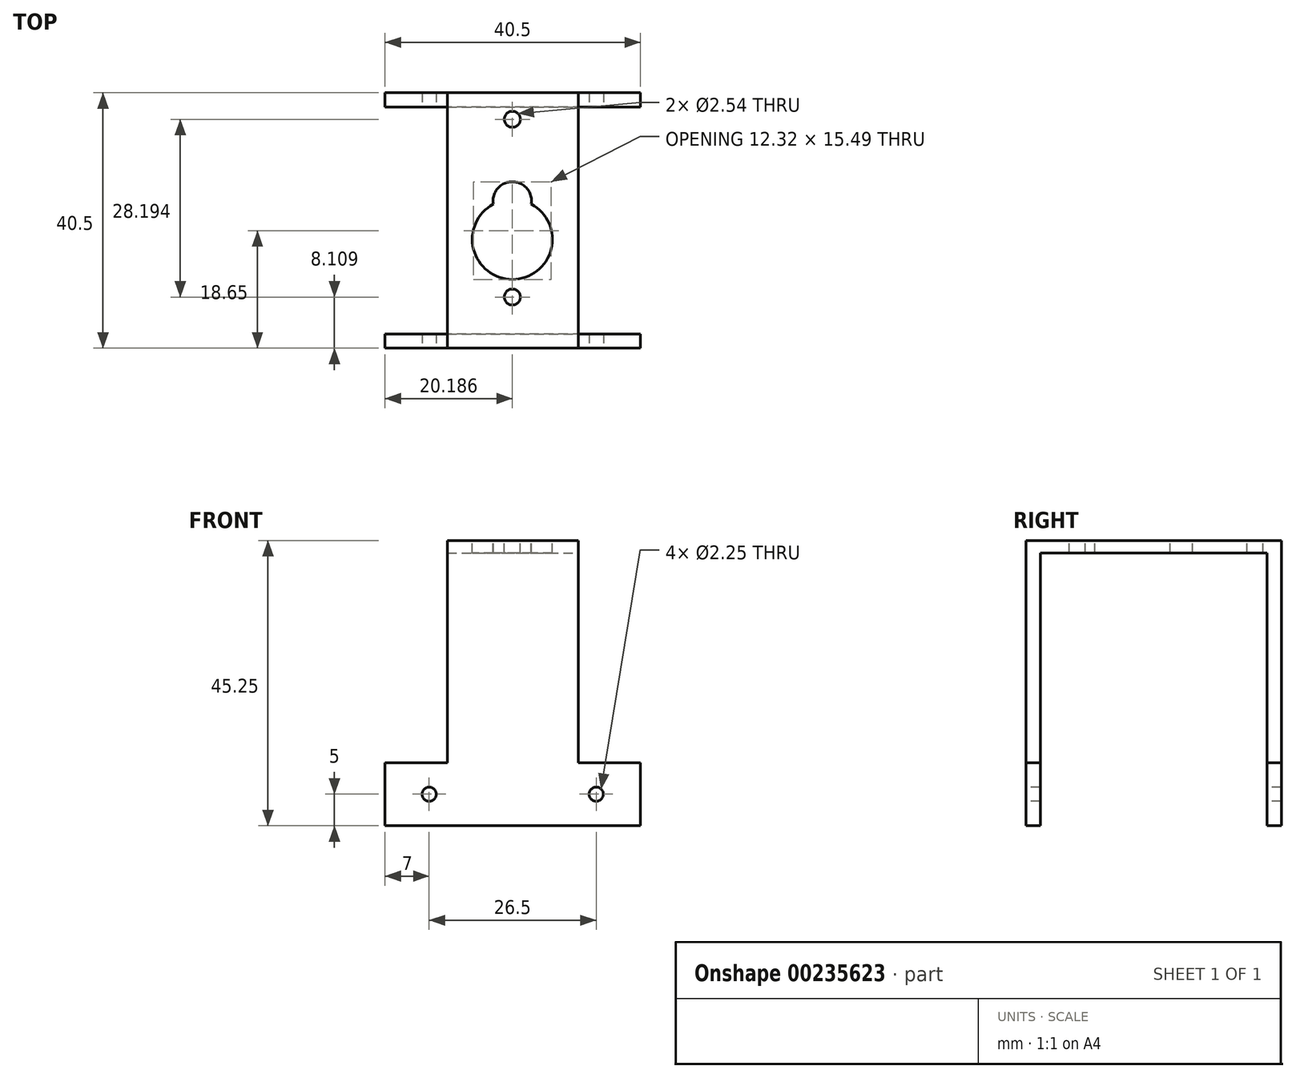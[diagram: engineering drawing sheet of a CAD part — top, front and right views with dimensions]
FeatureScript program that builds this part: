
annotation { "Feature Type Name" : "Feature", "Feature Type Description" : "" }
export const myFeature = defineFeature(function(context is Context, id is Id, definition is map)
    precondition{}
    {
        {
            var Q0;
            Q0=qCreatedBy(makeId("Top.planeOp"),FACE);
            var sketch = newSketch(context, id + "F0", { "sketchPlane" : qUnion([Q0])});
            skLineSegment(sketch, "E0.bottom", {"start": v(10.37, -20.25) * mm, "end": v(-10.38, -20.25) * mm});
            skLineSegment(sketch, "E0.top", {"start": v(10.38, 20.25) * mm, "end": v(-10.37, 20.25) * mm});
            skLineSegment(sketch, "E0.left", {"start": v(10.37, -20.25) * mm, "end": v(10.38, 20.25) * mm});
            skLineSegment(sketch, "E0.right", {"start": v(-10.38, -20.25) * mm, "end": v(-10.37, 20.25) * mm});
            skPoint(sketch, "E0.middle", {"position": v(0, 0) * mm});
            skSolve(sketch);
        }
        {
            var Q0;
            Q0=qCreatedBy(makeId("Front.planeOp"),FACE);
            var sketch = newSketch(context, id + "F1", { "sketchPlane" : qUnion([Q0])});
            skLineSegment(sketch, "E1.bottom", {"start": v(-10.38, 0) * mm, "end": v(10.37, 0) * mm});
            skLineSegment(sketch, "E1.top", {"start": v(-10.38, -33.25) * mm, "end": v(10.37, -33.25) * mm});
            skLineSegment(sketch, "E1.left", {"start": v(-10.38, 0) * mm, "end": v(-10.37, -33.25) * mm});
            skLineSegment(sketch, "E1.right", {"start": v(10.38, 0) * mm, "end": v(10.38, -33.25) * mm});
            skSolve(sketch);
        }
        {
            var Q0;
            Q0=makeQuery(id+"F0.imprint","IMPRINT",FACE,{"disambiguationData":[TD([[makeQuery(id+"F0.imprint","IMPRINT",EDGE,{"derivedFrom":sQuery(id+"F0.wireOp",EDGE,"E0.bottom")}),-1.0]])]});
            extrude(context, id + "F2", {"entities" : qUnion([Q0]), "depth" : 2 * mm});
        }
        {
            var Q0;
            Q0=makeQuery(id+"F1.imprint","IMPRINT",FACE,{"disambiguationData":[TD([[makeQuery(id+"F1.imprint","IMPRINT",EDGE,{"derivedFrom":sQuery(id+"F1.wireOp",EDGE,"E1.bottom")}),-1.0]])]});
            var Q1;
            Q1=makeQuery(id+"F2.opExtrude","SWEPT_FACE",FACE,{"disambiguationData":[OSD([sQuery(id+"F0.wireOp",EDGE,"E0.bottom")])]});
            extrude(context, id + "F3", {"entities" : qUnion([Q0]), "operationType" : NewBodyOperationType.ADD, "endBound" : BoundingType.UP_TO_SURFACE, "endBoundEntityFace" : qUnion([Q1]), "depth" : 11.94 * mm, "hasSecondDirection" : true, "secondDirectionOppositeDirection" : false, "secondDirectionDepth" : 18 * mm});
        }
        {
            var Q0;
            Q0=makeQuery(id+"F1.imprint","IMPRINT",FACE,{"disambiguationData":[TD([[makeQuery(id+"F1.imprint","IMPRINT",EDGE,{"derivedFrom":sQuery(id+"F1.wireOp",EDGE,"E1.bottom")}),-1.0]])]});
            var Q1;
            Q1=makeQuery(id+"F2.opExtrude","SWEPT_FACE",FACE,{"disambiguationData":[OSD([sQuery(id+"F0.wireOp",EDGE,"E0.top")])]});
            extrude(context, id + "F4", {"entities" : qUnion([Q0]), "operationType" : NewBodyOperationType.ADD, "endBound" : BoundingType.UP_TO_SURFACE, "oppositeDirection" : true, "endBoundEntityFace" : qUnion([Q1]), "depth" : 25.4 * mm, "hasSecondDirection" : true, "secondDirectionOppositeDirection" : true, "secondDirectionDepth" : 18 * mm});
        }
        {
            var Q0;
            Q0=makeQuery(id+"F4.boolean.opBoolean","MERGE",FACE,{"derivedFrom":[makeQuery(id+"F2.opExtrude","SWEPT_FACE",FACE,{"disambiguationData":[OSD([sQuery(id+"F0.wireOp",EDGE,"E0.top")])]}),makeQuery(id+"F4.opExtrude","CAP_FACE",FACE,{"disambiguationData":[OSD([sQuery(id+"F1.wireOp",EDGE,"E1.bottom"),sQuery(id+"F1.wireOp",EDGE,"E1.top"),sQuery(id+"F1.wireOp",EDGE,"E1.left"),sQuery(id+"F1.wireOp",EDGE,"E1.right")])],"isStart":false})]});
            var sketch = newSketch(context, id + "F5", { "sketchPlane" : qUnion([Q0])});
            skLineSegment(sketch, "E2", {"start": v(0, 2) * mm, "end": v(0, -33.25) * mm, "construction": true});
            skLineSegment(sketch, "E3.bottom", {"start": v(-20.25, -33.25) * mm, "end": v(20.25, -33.25) * mm});
            skLineSegment(sketch, "E3.top", {"start": v(-20.25, -43.25) * mm, "end": v(20.25, -43.25) * mm});
            skLineSegment(sketch, "E3.left", {"start": v(-20.25, -33.25) * mm, "end": v(-20.25, -43.25) * mm});
            skLineSegment(sketch, "E3.right", {"start": v(20.25, -33.25) * mm, "end": v(20.25, -43.25) * mm});
            skSolve(sketch);
        }
        {
            var Q0;
            Q0=makeQuery(id+"F5.imprint","IMPRINT",FACE,{"disambiguationData":[TD([[makeQuery(id+"F5.imprint","IMPRINT",EDGE,{"derivedFrom":sQuery(id+"F5.wireOp",EDGE,"E3.top")}),1.0]])]});
            var Q1;
            Q1=makeQuery(id+"F4.opExtrude","CAP_FACE",FACE,{"disambiguationData":[OSD([sQuery(id+"F1.wireOp",EDGE,"E1.bottom"),sQuery(id+"F1.wireOp",EDGE,"E1.top"),sQuery(id+"F1.wireOp",EDGE,"E1.left"),sQuery(id+"F1.wireOp",EDGE,"E1.right")])],"isStart":true});
            extrude(context, id + "F6", {"entities" : qUnion([Q0]), "operationType" : NewBodyOperationType.ADD, "endBound" : BoundingType.UP_TO_SURFACE, "oppositeDirection" : true, "endBoundEntityFace" : qUnion([Q1]), "depth" : 25.4 * mm});
        }
        {
            var Q0;
            Q0=makeQuery(id+"F3.boolean.opBoolean","MERGE",FACE,{"derivedFrom":[makeQuery(id+"F2.opExtrude","SWEPT_FACE",FACE,{"disambiguationData":[OSD([sQuery(id+"F0.wireOp",EDGE,"E0.bottom")])]}),makeQuery(id+"F3.opExtrude","CAP_FACE",FACE,{"disambiguationData":[OSD([sQuery(id+"F1.wireOp",EDGE,"E1.bottom"),sQuery(id+"F1.wireOp",EDGE,"E1.top"),sQuery(id+"F1.wireOp",EDGE,"E1.left"),sQuery(id+"F1.wireOp",EDGE,"E1.right")])],"isStart":false})]});
            var sketch = newSketch(context, id + "F7", { "sketchPlane" : qUnion([Q0])});
            skLineSegment(sketch, "E4.bottom", {"start": v(-20.25, -33.25) * mm, "end": v(20.25, -33.25) * mm});
            skLineSegment(sketch, "E4.top", {"start": v(-20.25, -43.25) * mm, "end": v(20.25, -43.25) * mm});
            skLineSegment(sketch, "E4.left", {"start": v(-20.25, -33.25) * mm, "end": v(-20.25, -43.25) * mm});
            skLineSegment(sketch, "E4.right", {"start": v(20.25, -33.25) * mm, "end": v(20.25, -43.25) * mm});
            skLineSegment(sketch, "E5", {"start": v(0, 2) * mm, "end": v(0, -33.25) * mm});
            skSolve(sketch);
        }
        {
            var Q0;
            Q0=qSketchRegion(id+"F7",true);
            var Q1;
            Q1=makeQuery(id+"F3.opExtrude","CAP_FACE",FACE,{"disambiguationData":[OSD([sQuery(id+"F1.wireOp",EDGE,"E1.bottom"),sQuery(id+"F1.wireOp",EDGE,"E1.top"),sQuery(id+"F1.wireOp",EDGE,"E1.left"),sQuery(id+"F1.wireOp",EDGE,"E1.right")])],"isStart":true});
            extrude(context, id + "F8", {"entities" : qUnion([Q0]), "operationType" : NewBodyOperationType.ADD, "endBound" : BoundingType.UP_TO_SURFACE, "oppositeDirection" : true, "endBoundEntityFace" : qUnion([Q1]), "depth" : 25.4 * mm});
        }
        {
            var Q0;
            Q0=makeQuery(id+"F8.boolean.opBoolean","MERGE",FACE,{"derivedFrom":[makeQuery(id+"F3.boolean.opBoolean","MERGE",FACE,{"derivedFrom":[makeQuery(id+"F2.opExtrude","SWEPT_FACE",FACE,{"disambiguationData":[OSD([sQuery(id+"F0.wireOp",EDGE,"E0.bottom")])]}),makeQuery(id+"F3.opExtrude","CAP_FACE",FACE,{"disambiguationData":[OSD([sQuery(id+"F1.wireOp",EDGE,"E1.bottom"),sQuery(id+"F1.wireOp",EDGE,"E1.top"),sQuery(id+"F1.wireOp",EDGE,"E1.left"),sQuery(id+"F1.wireOp",EDGE,"E1.right")])],"isStart":false})]}),makeQuery(id+"F8.opExtrude","CAP_FACE",FACE,{"disambiguationData":[OSD([sQuery(id+"F7.wireOp",EDGE,"E4.bottom"),sQuery(id+"F7.wireOp",EDGE,"E4.top"),sQuery(id+"F7.wireOp",EDGE,"E4.left"),sQuery(id+"F7.wireOp",EDGE,"E4.right")])],"isStart":true})]});
            var sketch = newSketch(context, id + "F9", { "sketchPlane" : qUnion([Q0])});
            skLineSegment(sketch, "E6", {"start": v(-20.25, -38.25) * mm, "end": v(-13.25, -38.25) * mm, "construction": true});
            skLineSegment(sketch, "E7", {"start": v(20.25, -38.25) * mm, "end": v(13.25, -38.25) * mm, "construction": true});
            skCircle(sketch, "E8", {"center": v(-13.25, -38.25) * mm, "radius": 1.13 * mm});
            skCircle(sketch, "E9", {"center": v(13.25, -38.25) * mm, "radius": 1.13 * mm});
            skSolve(sketch);
        }
        {
            var Q0;
            Q0=makeQuery(id+"F9.imprint","IMPRINT",FACE,{"disambiguationData":[TD([[makeQuery(id+"F9.imprint","IMPRINT",EDGE,{"derivedFrom":sQuery(id+"F9.wireOp",EDGE,"E8")}),1.0]])]});
            var Q1;
            Q1=makeQuery(id+"F9.imprint","IMPRINT",FACE,{"disambiguationData":[TD([[makeQuery(id+"F9.imprint","IMPRINT",EDGE,{"derivedFrom":sQuery(id+"F9.wireOp",EDGE,"E9")}),1.0]])]});
            var Q2;
            Q2=sQuery(id+"F9.wireOp",EDGE,"E8");
            var Q3;
            Q3=sQuery(id+"F9.wireOp",EDGE,"E9");
            extrude(context, id + "F10", {"entities" : qUnion([Q0, Q1]), "operationType" : NewBodyOperationType.REMOVE, "surfaceEntities" : qUnion([Q2, Q3]), "endBound" : BoundingType.THROUGH_ALL, "oppositeDirection" : true, "depth" : 25.4 * mm});
        }
        {
            var Q0;
            Q0=makeQuery(id+"F2.opExtrude","CAP_FACE",FACE,{"disambiguationData":[OSD([sQuery(id+"F0.wireOp",EDGE,"E0.bottom"),sQuery(id+"F0.wireOp",EDGE,"E0.top"),sQuery(id+"F0.wireOp",EDGE,"E0.left"),sQuery(id+"F0.wireOp",EDGE,"E0.right")])],"isStart":false});
            var sketch = newSketch(context, id + "F11", { "sketchPlane" : qUnion([Q0])});
            skCircle(sketch, "E10", {"center": v(-0.06, -3) * mm, "radius": 6.35 * mm});
            skCircle(sketch, "E11", {"center": v(-0.06, 3.1) * mm, "radius": 3.05 * mm});
            skCircle(sketch, "E12", {"center": v(-0.06, 16.05) * mm, "radius": 1.27 * mm});
            skCircle(sketch, "E13", {"center": v(-0.06, -12.14) * mm, "radius": 1.27 * mm});
            skLineSegment(sketch, "E14", {"start": v(-0.06, 16.05) * mm, "end": v(-0.06, 3.1) * mm, "construction": true});
            skLineSegment(sketch, "E15", {"start": v(-0.06, 3.1) * mm, "end": v(-0.06, -12.14) * mm, "construction": true});
            skSolve(sketch);
        }
        {
            var Q0;
            {var subQ0=sQuery(id+"F11.wireOp",EDGE,"E11");var subQ1=sQuery(id+"F11.wireOp",EDGE,"E10");var subQ2=makeQuery(id+"F11.imprint","INTERSECT",VERTEX,{"disambiguationData":[OD(0.0)],"derivedFrom":[subQ1,subQ0]});Q0=makeQuery(id+"F11.imprint","IMPRINT",FACE,{"disambiguationData":[TD([[makeQuery(id+"F11.imprint","IMPRINT",EDGE,{"disambiguationData":[TD([[subQ2,-1.0]])],"derivedFrom":subQ1}),1.0]])]});}
            var Q1;
            {var subQ0=sQuery(id+"F11.wireOp",EDGE,"E11");var subQ1=sQuery(id+"F11.wireOp",EDGE,"E10");var subQ2=makeQuery(id+"F11.imprint","INTERSECT",VERTEX,{"disambiguationData":[OD(0.0)],"derivedFrom":[subQ1,subQ0]});Q1=makeQuery(id+"F11.imprint","IMPRINT",FACE,{"disambiguationData":[TD([[makeQuery(id+"F11.imprint","IMPRINT",EDGE,{"disambiguationData":[TD([[subQ2,1.0]])],"derivedFrom":subQ1}),-1.0]])]});}
            var Q2;
            {var subQ0=sQuery(id+"F11.wireOp",EDGE,"E11");var subQ1=sQuery(id+"F11.wireOp",EDGE,"E10");var subQ2=makeQuery(id+"F11.imprint","INTERSECT",VERTEX,{"disambiguationData":[OD(0.0)],"derivedFrom":[subQ1,subQ0]});Q2=makeQuery(id+"F11.imprint","IMPRINT",FACE,{"disambiguationData":[TD([[makeQuery(id+"F11.imprint","IMPRINT",EDGE,{"disambiguationData":[TD([[subQ2,1.0]])],"derivedFrom":subQ1}),1.0]])]});}
            var Q3;
            Q3=makeQuery(id+"F11.imprint","IMPRINT",FACE,{"disambiguationData":[TD([[makeQuery(id+"F11.imprint","IMPRINT",EDGE,{"derivedFrom":sQuery(id+"F11.wireOp",EDGE,"E13")}),1.0]])]});
            var Q4;
            Q4=makeQuery(id+"F11.imprint","IMPRINT",FACE,{"disambiguationData":[TD([[makeQuery(id+"F11.imprint","IMPRINT",EDGE,{"derivedFrom":sQuery(id+"F11.wireOp",EDGE,"E12")}),1.0]])]});
            var Q5;
            Q5=makeQuery(id+"F2.opExtrude","CAP_FACE",FACE,{"disambiguationData":[OSD([sQuery(id+"F0.wireOp",EDGE,"E0.bottom"),sQuery(id+"F0.wireOp",EDGE,"E0.top"),sQuery(id+"F0.wireOp",EDGE,"E0.left"),sQuery(id+"F0.wireOp",EDGE,"E0.right")])],"isStart":true});
            extrude(context, id + "F12", {"entities" : qUnion([Q0, Q1, Q2, Q3, Q4]), "operationType" : NewBodyOperationType.REMOVE, "endBound" : BoundingType.UP_TO_SURFACE, "oppositeDirection" : true, "endBoundEntityFace" : qUnion([Q5]), "depth" : 25.4 * mm});
        }
    });
